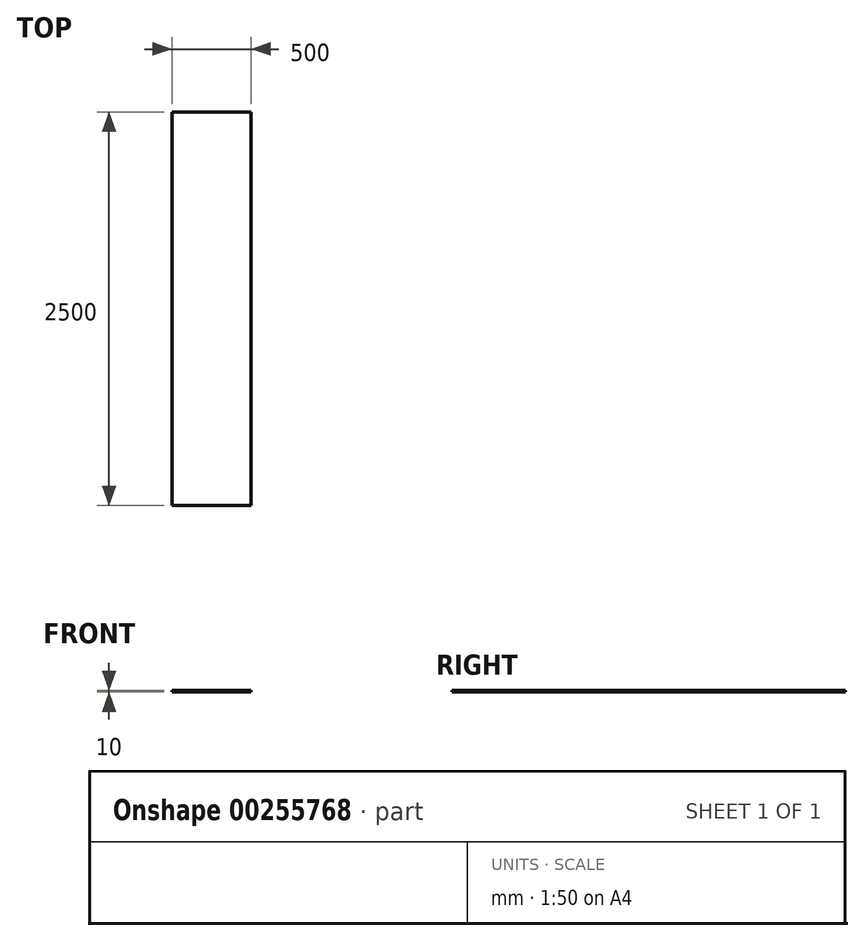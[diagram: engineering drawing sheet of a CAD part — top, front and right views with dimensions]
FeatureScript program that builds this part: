
annotation { "Feature Type Name" : "Feature", "Feature Type Description" : "" }
export const myFeature = defineFeature(function(context is Context, id is Id, definition is map)
    precondition{}
    {
        {
            var Q0;
            Q0=qCreatedBy(makeId("Top.planeOp"),FACE);
            var sketch = newSketch(context, id + "F0", { "sketchPlane" : qUnion([Q0])});
            skLineSegment(sketch, "E0.bottom", {"start": v(250, -1250) * mm, "end": v(-250, -1250) * mm});
            skLineSegment(sketch, "E0.top", {"start": v(250, 1250) * mm, "end": v(-250, 1250) * mm});
            skLineSegment(sketch, "E0.left", {"start": v(250, -1250) * mm, "end": v(250, 1250) * mm});
            skLineSegment(sketch, "E0.right", {"start": v(-250, -1250) * mm, "end": v(-250, 1250) * mm});
            skPoint(sketch, "E0.middle", {"position": v(0, 0) * mm});
            skSolve(sketch);
        }
        {
            var Q0;
            Q0 = qSketchRegion(id + "F0", true);
            extrude(context, id + "F1", {"entities" : qUnion([Q0]), "endBound" : BoundingType.SYMMETRIC, "depth" : 10 * mm, "offsetDistance" : 25 * mm});
        }
    });
